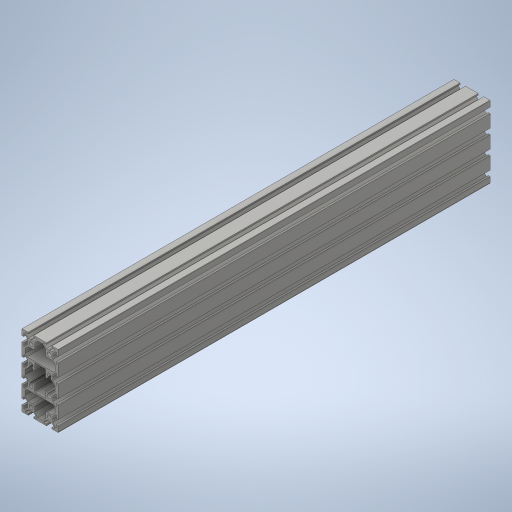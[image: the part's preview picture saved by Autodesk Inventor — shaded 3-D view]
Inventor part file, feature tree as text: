
AUTODESK INVENTOR PART (.ipt)
format: ipt  version: 2024 (Build 280153000, 153)  size: 625,152 bytes
history: native  units: mm
features: thread x16, sketch x2, extrude x1, hole x1, pattern_linear x1
ambient origin geometry x8: Origin, YZ Plane, XZ Plane, XY Plane, X Axis, Y Axis, Z Axis, Center Point
bodies: Solid1 (feature_tree)
feature tree (21):
  extrude  "Extrusion1"  Depth=20.0mm
  hole  "Hole1"  [1 undecoded]
  pattern_linear  "Rectangular Pattern1"  Spacing1=10.0mm  [1 undecoded]
  thread  "Thread2"  [1 undecoded]
  thread  "Thread3"  [1 undecoded]
  thread  "Thread4"  [1 undecoded]
  thread  "Thread5"  [1 undecoded]
  thread  "Thread6"  [1 undecoded]
  thread  "Thread7"  [1 undecoded]
  thread  "Thread8"  [1 undecoded]
  thread  "Thread9"  [1 undecoded]
  thread  "Thread10"  [1 undecoded]
  thread  "Thread11"  [1 undecoded]
  thread  "Thread12"  [1 undecoded]
  thread  "Thread13"  [1 undecoded]
  thread  "Thread14"  [1 undecoded]
  thread  "Thread15"  [1 undecoded]
  thread  "Thread16"  [1 undecoded]
  thread  "Thread17"  [1 undecoded]
  sketch  "Sketch_118"  dims[d2=4.2mm d3=6.0mm d4=4.0mm d5=2.0mm d6=90.0deg d7=425.0mm d8=0.0mm d9=20.0mm d11=20.0mm d12=20.0mm d14=60.0mm d17=10.0mm d18=0.0mm d19=10.0mm d20=0.0mm d21=10.0mm d22=0.0mm d23=10.0mm d24=0.0mm d25=10.0mm d26=0.0mm d27=10.0mm d28=0.0mm d29=10.0mm d30=0.0mm d31=10.0mm d32=0.0mm d33=10.0mm d34=0.0mm d35=10.0mm d36=0.0mm d37=10.0mm d38=0.0mm d39=10.0mm d40=0.0mm d41=10.0mm d42=0.0mm d43=10.0mm d44=0.0mm d45=10.0mm d46=0.0mm d47=10.0mm d48=0.0mm]
  sketch  "Sketch2"  dims[d0=475.0mm d1=0.0mm]
note: 18 required parameter values undecoded (feature->parameter linkage not recoverable at this tier; creation-order binding heuristic only, values carry confidence <= 0.55)
